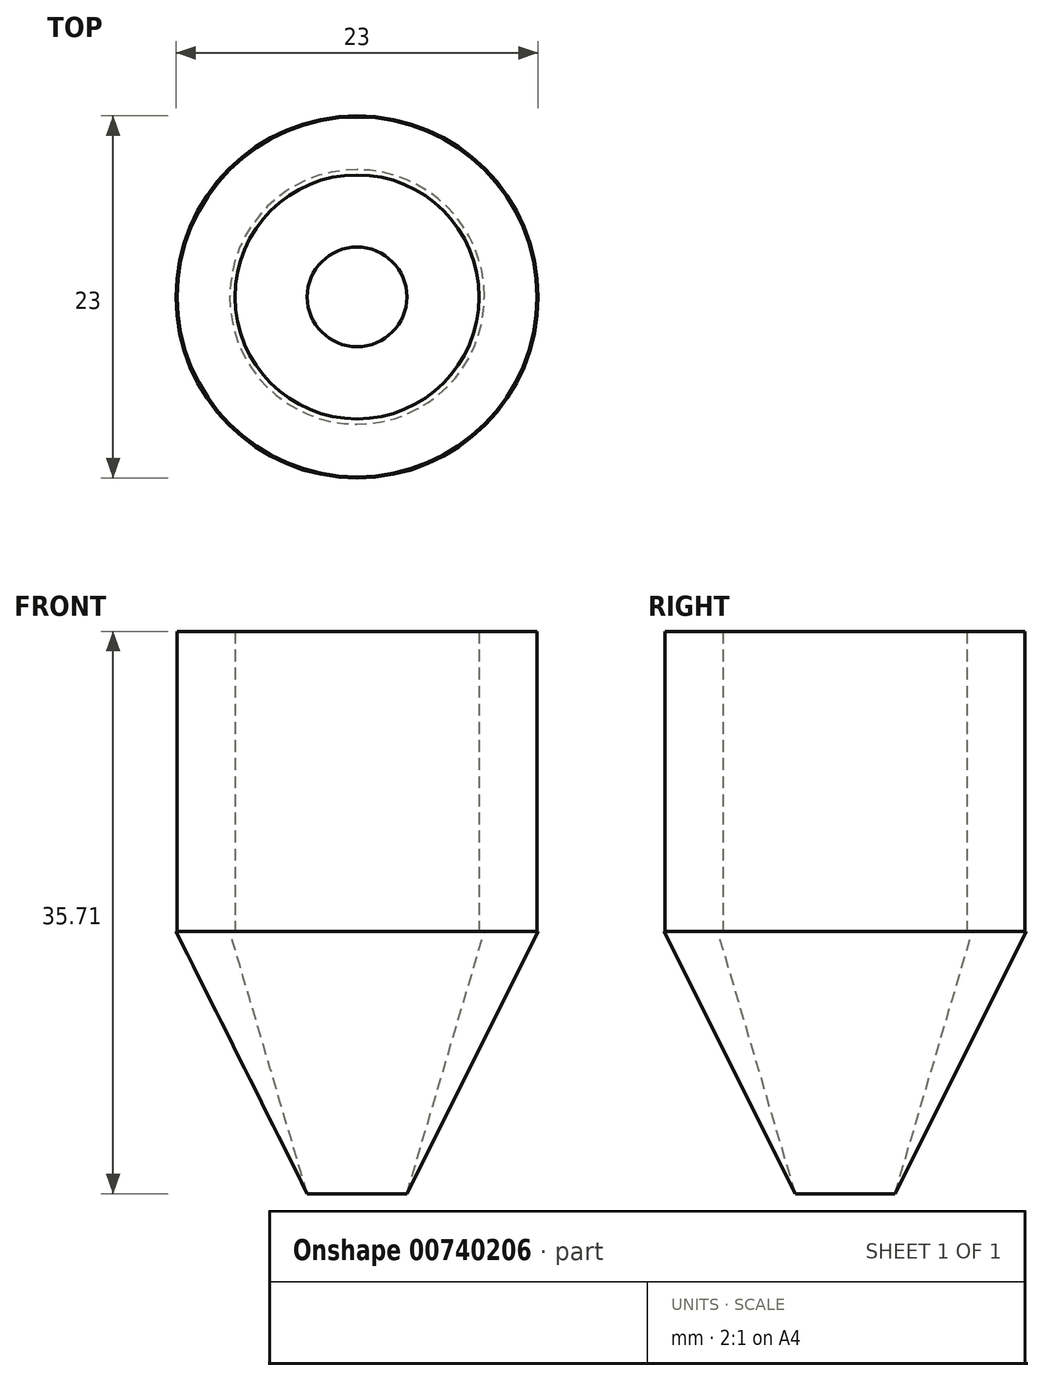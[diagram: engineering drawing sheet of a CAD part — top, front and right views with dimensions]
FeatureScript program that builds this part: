
annotation { "Feature Type Name" : "Feature", "Feature Type Description" : "" }
export const myFeature = defineFeature(function(context is Context, id is Id, definition is map)
    precondition{}
    {
        {
            var Q0;
            Q0=qCreatedBy(makeId("Top.planeOp"),FACE);
            var sketch = newSketch(context, id + "F0", { "sketchPlane" : qUnion([Q0])});
            skCircle(sketch, "E0", {"center": v(0, 0) * mm, "radius": 11.43 * mm});
            skSolve(sketch);
        }
        {
            var Q0;
            Q0=makeQuery(id+"F0.imprint","IMPRINT",FACE,{"disambiguationData":[TD([[makeQuery(id+"F0.imprint","IMPRINT",EDGE,{"derivedFrom":sQuery(id+"F0.wireOp",EDGE,"E0")}),1.0]])]});
            extrude(context, id + "F1", {"entities" : qUnion([Q0]), "depth" : 19.05 * mm, "offsetDistance" : 25.4 * mm});
        }
        {
            var Q0;
            Q0=makeQuery(id+"F1.opExtrude","CAP_FACE",FACE,{"disambiguationData":[OSD([sQuery(id+"F0.wireOp",EDGE,"E0")])],"isStart":true});
            var sketch = newSketch(context, id + "F2", { "sketchPlane" : qUnion([Q0])});
            skCircle(sketch, "E1", {"center": v(0, 0) * mm, "radius": 7.75 * mm});
            skSolve(sketch);
        }
        {
            var Q0;
            Q0=makeQuery(id+"F2.imprint","IMPRINT",FACE,{"disambiguationData":[TD([[makeQuery(id+"F2.imprint","IMPRINT",EDGE,{"derivedFrom":sQuery(id+"F2.wireOp",EDGE,"E1")}),1.0]])]});
            extrude(context, id + "F3", {"entities" : qUnion([Q0]), "operationType" : NewBodyOperationType.REMOVE, "oppositeDirection" : true, "depth" : 19.05 * mm, "offsetDistance" : 25.4 * mm});
        }
        {
            var Q0;
            Q0=qCreatedBy(makeId("Front.planeOp"),FACE);
            var sketch = newSketch(context, id + "F4", { "sketchPlane" : qUnion([Q0])});
            skLineSegment(sketch, "E2", {"start": v(11.5, 0) * mm, "end": v(0, -22.98) * mm});
            skLineSegment(sketch, "E3", {"start": v(0, -22.98) * mm, "end": v(0, 0) * mm});
            skLineSegment(sketch, "E4", {"start": v(0, 0) * mm, "end": v(11.5, 0) * mm});
            skSolve(sketch);
        }
        {
            var Q0;
            Q0 = qSketchRegion(id + "F4", true);
            var Q1;
            Q1=sQuery(id+"F4.wireOp",EDGE,"E3");
            revolve(context, id + "F5", {"operationType" : NewBodyOperationType.ADD, "surfaceOperationType" : NewSurfaceOperationType.NEW, "entities" : qUnion([Q0]), "axis" : qUnion([Q1]), "revolveType" : RevolveType.FULL});
        }
        {
            var Q0;
            Q0=qCreatedBy(makeId("Right.planeOp"),FACE);
            var sketch = newSketch(context, id + "F6", { "sketchPlane" : qUnion([Q0])});
            skLineSegment(sketch, "E5", {"start": v(-8.09, 0) * mm, "end": v(0, -27.37) * mm});
            skLineSegment(sketch, "E6", {"start": v(0, -27.37) * mm, "end": v(0, 0) * mm});
            skLineSegment(sketch, "E7", {"start": v(-8.09, 0) * mm, "end": v(0, 0) * mm});
            skSolve(sketch);
        }
        {
            var Q0;
            Q0 = qSketchRegion(id + "F6", true);
            var Q1;
            Q1=sQuery(id+"F6.wireOp",EDGE,"E6");
            revolve(context, id + "F7", {"operationType" : NewBodyOperationType.REMOVE, "surfaceOperationType" : NewSurfaceOperationType.NEW, "entities" : qUnion([Q0]), "axis" : qUnion([Q1]), "revolveType" : RevolveType.FULL});
        }
    });
